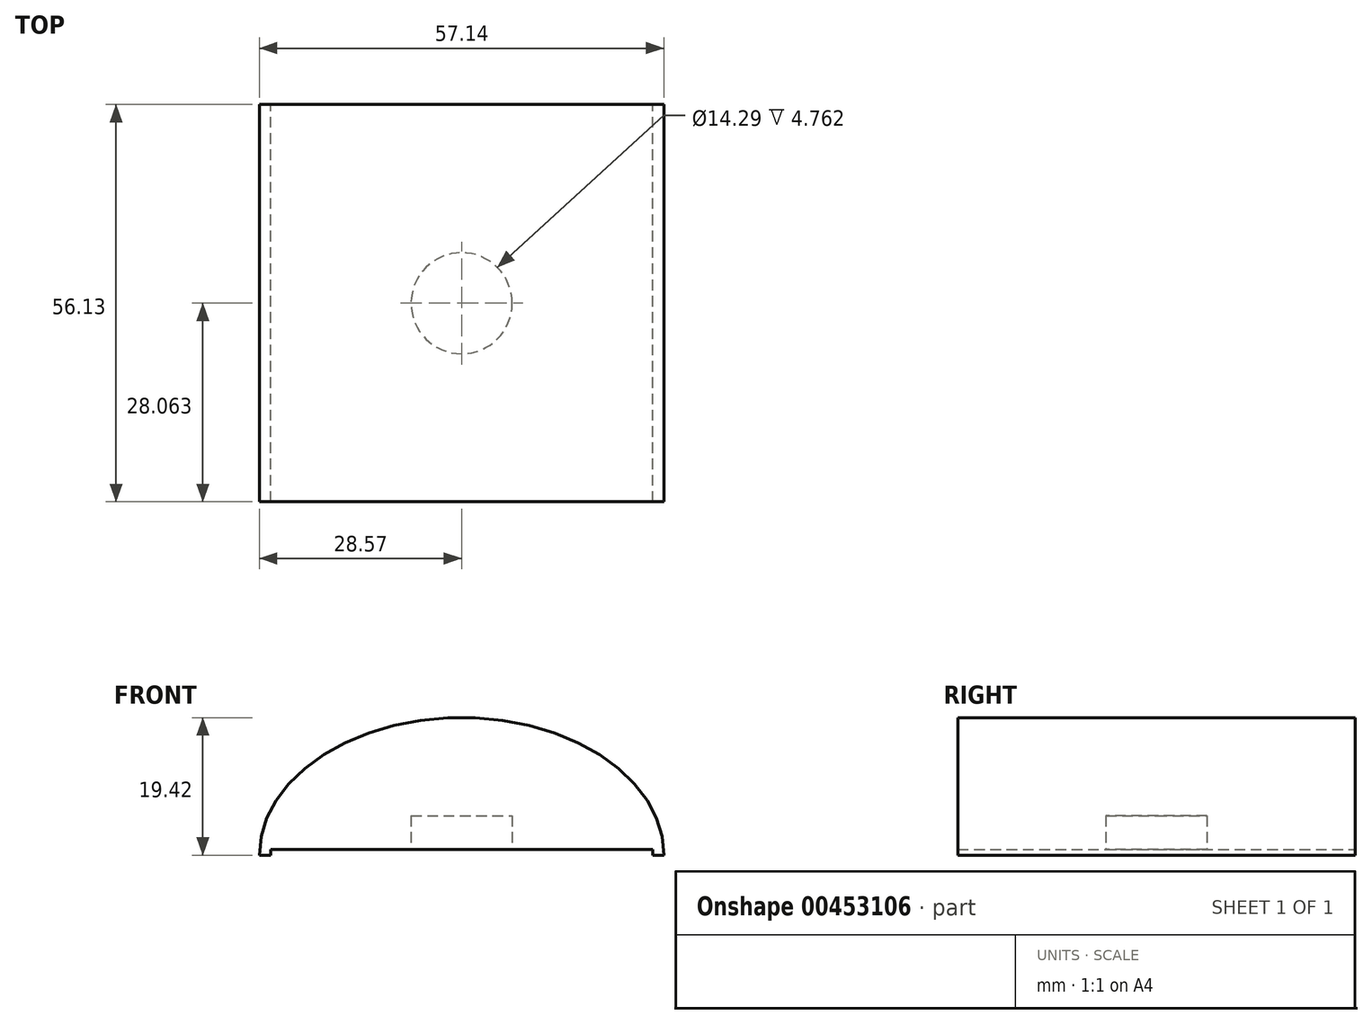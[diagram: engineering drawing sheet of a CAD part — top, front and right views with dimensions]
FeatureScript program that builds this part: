
annotation { "Feature Type Name" : "Feature", "Feature Type Description" : "" }
export const myFeature = defineFeature(function(context is Context, id is Id, definition is map)
    precondition{}
    {
        {
            var Q0;
            Q0=qCreatedBy(makeId("Front.planeOp"),FACE);
            var sketch = newSketch(context, id + "F0", { "sketchPlane" : qUnion([Q0])});
            skLineSegment(sketch, "E0", {"start": v(-28.58, 11.74) * mm, "end": v(-26.99, 11.74) * mm});
            skEllipticalArc(sketch, "E1", {});
            skLineSegment(sketch, "E2", {"start": v(-26.99, 11.74) * mm, "end": v(-26.99, 12.54) * mm});
            skLineSegment(sketch, "E3", {"start": v(-26.99, 12.54) * mm, "end": v(0, 12.54) * mm});
            skLineSegment(sketch, "E4.MirrorCS", {"start": v(26.99, 12.54) * mm, "end": v(0, 12.54) * mm});
            skLineSegment(sketch, "E5.MirrorCS", {"start": v(26.99, 11.74) * mm, "end": v(26.99, 12.54) * mm});
            skLineSegment(sketch, "E6.trimOffspring", {"start": v(26.99, 11.74) * mm, "end": v(28.58, 11.74) * mm});
            const initialGuessF0  = {"E1": [0, 0.0117431515827775, -1, 0, 0.028575, 0.019415342248976255, 3.141592653589793, 0]};
            skSetInitialGuess(sketch, initialGuessF0);
            skSolve(sketch);
        }
        {
            var Q0;
            Q0 = qSketchRegion(id + "F0", true);
            extrude(context, id + "F1", {"entities" : qUnion([Q0]), "depth" : 56.13 * mm});
        }
        {
            var Q0;
            Q0=makeQuery(id+"F1.opExtrude","SWEPT_FACE",FACE,{"disambiguationData":[OSD([sQuery(id+"F0.wireOp",EDGE,"E3"),sQuery(id+"F0.wireOp",EDGE,"E4.MirrorCS")])]});
            var sketch = newSketch(context, id + "F2", { "sketchPlane" : qUnion([Q0])});
            skLineSegment(sketch, "E7", {"start": v(0, 56.13) * mm, "end": v(0, 0) * mm, "construction": true});
            skCircle(sketch, "E8", {"center": v(0, 28.07) * mm, "radius": 7.14 * mm});
            skSolve(sketch);
        }
        {
            var Q0;
            Q0=makeQuery(id+"F2.imprint","IMPRINT",FACE,{"disambiguationData":[TD([[makeQuery(id+"F2.imprint","IMPRINT",EDGE,{"derivedFrom":sQuery(id+"F2.wireOp",EDGE,"E8")}),1.0]])]});
            extrude(context, id + "F3", {"entities" : qUnion([Q0]), "operationType" : NewBodyOperationType.REMOVE, "oppositeDirection" : true, "depth" : 4.76 * mm});
        }
    });
